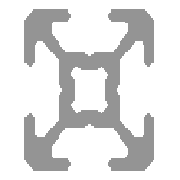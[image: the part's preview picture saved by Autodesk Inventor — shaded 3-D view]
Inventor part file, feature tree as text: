
AUTODESK INVENTOR PART (.ipt)
format: ipt  version: 2015 (Build 190159000, 159)  size: 385,536 bytes
history: native  units: mm
features: other x3, extrude x1, sketch x1
ambient origin geometry x8: Origin, YZ Plane, XZ Plane, XY Plane, X Axis, Y Axis, Z Axis, Center Point
bodies: Body1 (feature_tree)
feature tree (5):
  other  "Blocks"
  extrude  "Extrusion3"  [1 undecoded]
  sketch  "Sketch1"  dims[d23=0.0mm]
  other  "20x20"
  other  "20x20:1"
note: 1 required parameter value undecoded (feature->parameter linkage not recoverable at this tier; creation-order binding heuristic only, values carry confidence <= 0.55)
